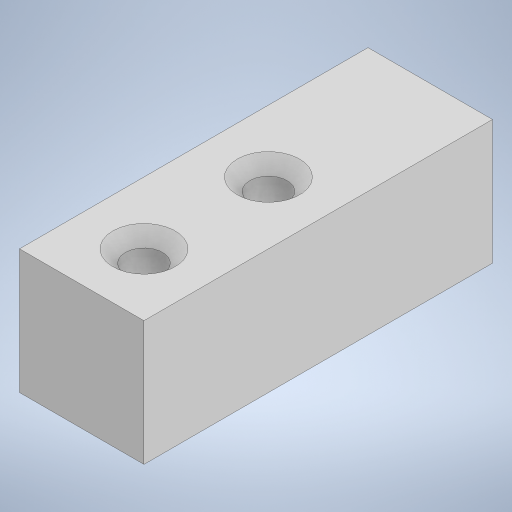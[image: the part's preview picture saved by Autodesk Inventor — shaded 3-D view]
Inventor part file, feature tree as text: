
AUTODESK INVENTOR PART (.ipt)
format: ipt  version: 2023 (Build 270158000, 158)  size: 207,360 bytes
history: native  units: mm
features: other x1, extrude x1, chamfer x1, sketch x1
ambient origin geometry x8: Origin, YZ Plane, XZ Plane, XY Plane, X Axis, Y Axis, Z Axis, Center Point
bodies: Body1 (feature_tree)
feature tree (4):
  other  "Твердое тело1"
  extrude  "Выдавливание1"  Depth=10.0mm
  chamfer  "Фаска1"  Distance=28.0mm
  sketch  "Эскиз1"
